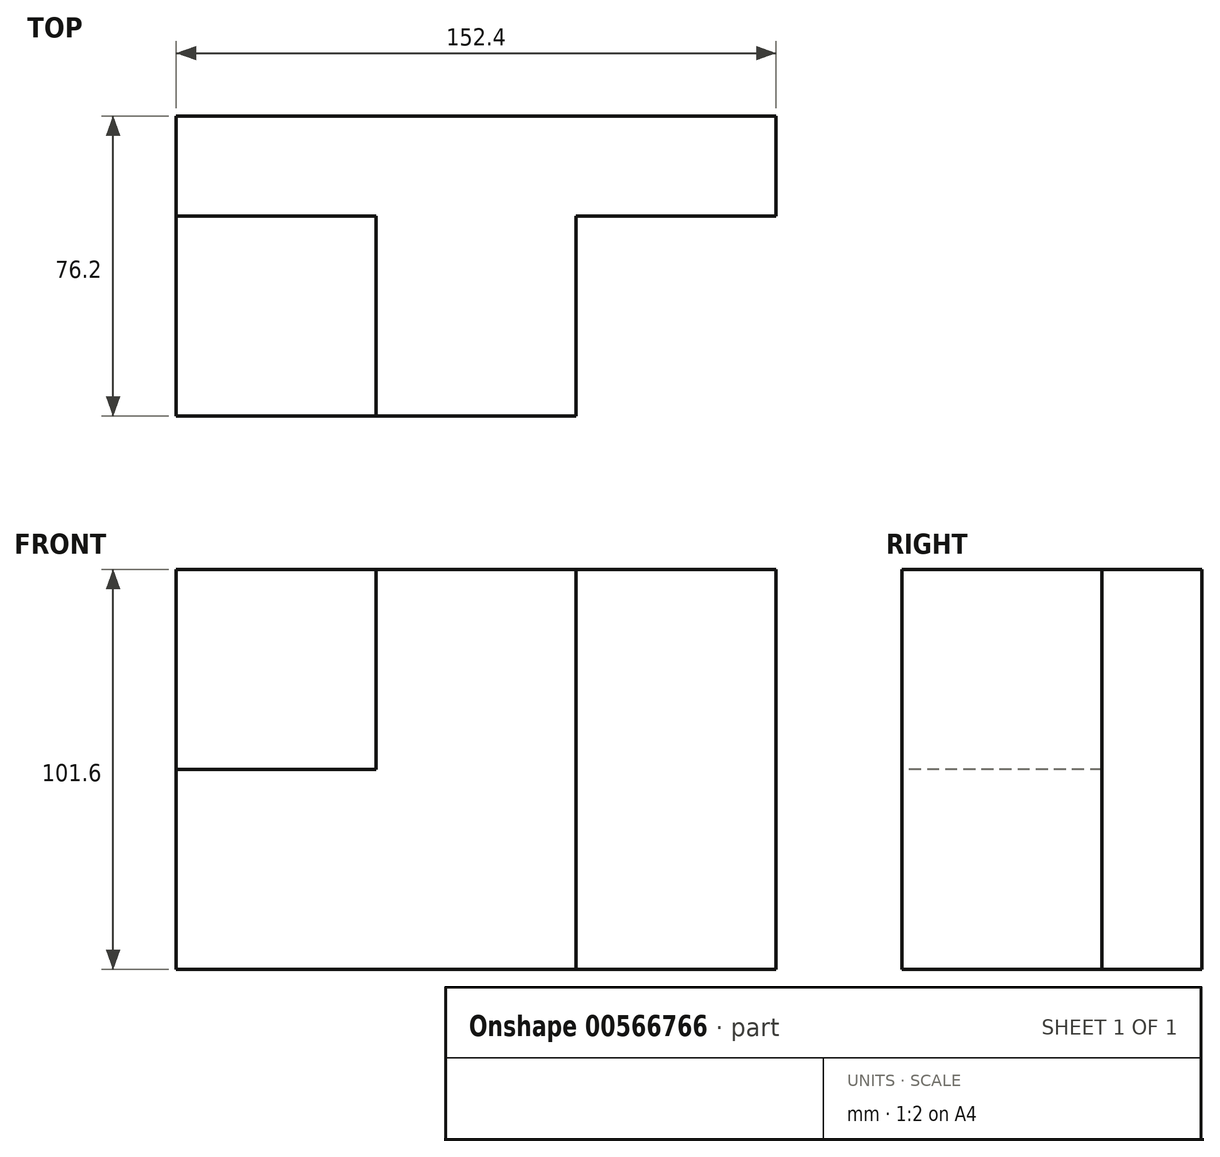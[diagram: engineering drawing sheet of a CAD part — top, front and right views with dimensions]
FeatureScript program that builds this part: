
annotation { "Feature Type Name" : "Feature", "Feature Type Description" : "" }
export const myFeature = defineFeature(function(context is Context, id is Id, definition is map)
    precondition{}
    {
        {
            var Q0;
            Q0=qCreatedBy(makeId("Top.planeOp"),FACE);
            var sketch = newSketch(context, id + "F0", { "sketchPlane" : qUnion([Q0])});
            skLineSegment(sketch, "E0.bottom", {"start": v(-57.13, 60.03) * mm, "end": v(95.27, 60.03) * mm});
            skLineSegment(sketch, "E0.top", {"start": v(-57.13, -16.17) * mm, "end": v(95.27, -16.17) * mm});
            skLineSegment(sketch, "E0.left", {"start": v(-57.13, 60.03) * mm, "end": v(-57.13, -16.17) * mm});
            skLineSegment(sketch, "E0.right", {"start": v(95.27, 60.03) * mm, "end": v(95.27, -16.17) * mm});
            skSolve(sketch);
        }
        {
            var Q0;
            Q0=makeQuery(id+"F0.imprint","IMPRINT",FACE,{"disambiguationData":[TD([[makeQuery(id+"F0.imprint","IMPRINT",EDGE,{"derivedFrom":sQuery(id+"F0.wireOp",EDGE,"E0.bottom")}),-1.0]])]});
            extrude(context, id + "F1", {"entities" : qUnion([Q0]), "depth" : 101.6 * mm, "offsetDistance" : 25.4 * mm});
        }
        {
            var Q0;
            Q0=makeQuery(id+"F1.opExtrude","SWEPT_FACE",FACE,{"disambiguationData":[OSD([sQuery(id+"F0.wireOp",EDGE,"E0.top")])]});
            var sketch = newSketch(context, id + "F2", { "sketchPlane" : qUnion([Q0])});
            skLineSegment(sketch, "E1.bottom", {"start": v(-57.13, 50.8) * mm, "end": v(-6.33, 50.8) * mm});
            skLineSegment(sketch, "E1.top", {"start": v(-57.13, 0) * mm, "end": v(-6.33, 0) * mm});
            skLineSegment(sketch, "E1.left", {"start": v(-57.13, 50.8) * mm, "end": v(-57.13, 0) * mm});
            skLineSegment(sketch, "E1.right", {"start": v(-6.33, 50.8) * mm, "end": v(-6.33, 0) * mm});
            skLineSegment(sketch, "E2.bottom", {"start": v(-6.33, 101.6) * mm, "end": v(44.47, 101.6) * mm});
            skLineSegment(sketch, "E2.top", {"start": v(-6.33, 0) * mm, "end": v(44.47, 0) * mm});
            skLineSegment(sketch, "E2.left", {"start": v(-6.33, 101.6) * mm, "end": v(-6.33, 0) * mm});
            skLineSegment(sketch, "E2.right", {"start": v(44.47, 101.6) * mm, "end": v(44.47, 0) * mm});
            skLineSegment(sketch, "E3.bottom", {"start": v(44.47, 50.8) * mm, "end": v(95.27, 50.8) * mm});
            skLineSegment(sketch, "E3.top", {"start": v(44.47, 0) * mm, "end": v(95.27, 0) * mm});
            skLineSegment(sketch, "E3.left", {"start": v(44.47, 50.8) * mm, "end": v(44.47, 0) * mm});
            skLineSegment(sketch, "E3.right", {"start": v(95.27, 50.8) * mm, "end": v(95.27, 0) * mm});
            skSolve(sketch);
        }
        {
            var Q0;
            {var subQ0=sQuery(id+"F2.wireOp",EDGE,"E1.bottom");Q0=makeQuery(id+"F2.imprint","IMPRINT",FACE,{"disambiguationData":[TD([[makeQuery(id+"F2.imprint","IMPRINT",EDGE,{"derivedFrom":subQ0}),1.0]])]});}
            var Q1;
            {var subQ0=sQuery(id+"F2.wireOp",EDGE,"E2.right");Q1=makeQuery(id+"F2.imprint","IMPRINT",FACE,{"disambiguationData":[TD([[makeQuery(id+"F2.imprint","IMPRINT",EDGE,{"derivedFrom":subQ0}),1.0]])]});}
            extrude(context, id + "F3", {"entities" : qUnion([Q0, Q1]), "operationType" : NewBodyOperationType.REMOVE, "oppositeDirection" : true, "depth" : 50.8 * mm, "offsetDistance" : 25.4 * mm});
        }
    });
